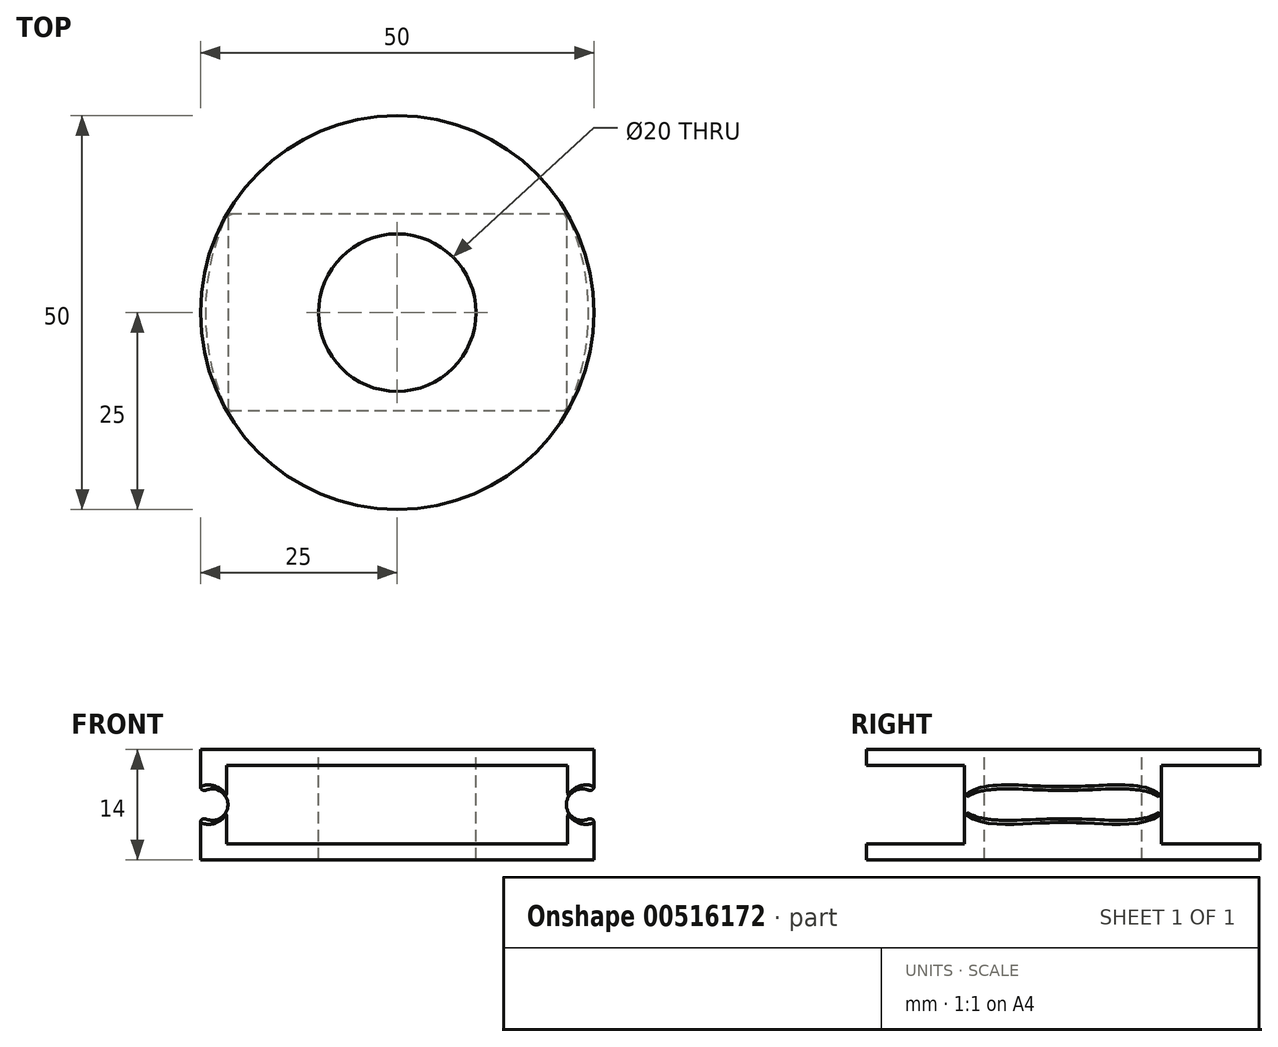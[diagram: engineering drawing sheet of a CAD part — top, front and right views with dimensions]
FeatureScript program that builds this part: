
annotation { "Feature Type Name" : "Feature", "Feature Type Description" : "" }
export const myFeature = defineFeature(function(context is Context, id is Id, definition is map)
    precondition{}
    {
        {
            var Q0;
            Q0=qCreatedBy(makeId("Right.planeOp"),FACE);
            var sketch = newSketch(context, id + "F0", { "sketchPlane" : qUnion([Q0])});
            skLineSegment(sketch, "E0.bottom", {"start": v(0, 0) * mm, "end": v(-50, 0) * mm});
            skLineSegment(sketch, "E0.top", {"start": v(0, 2) * mm, "end": v(-12.5, 2) * mm});
            skLineSegment(sketch, "E0.left", {"start": v(0, 0) * mm, "end": v(0, 2) * mm});
            skLineSegment(sketch, "E0.right", {"start": v(-50, 0) * mm, "end": v(-50, 2) * mm});
            skLineSegment(sketch, "E1.left", {"start": v(-12.5, 2) * mm, "end": v(-12.5, 12) * mm});
            skLineSegment(sketch, "E1.right", {"start": v(-37.5, 2) * mm, "end": v(-37.5, 12) * mm});
            skLineSegment(sketch, "E2.bottom", {"start": v(0, 12) * mm, "end": v(-12.5, 12) * mm});
            skLineSegment(sketch, "E2.top", {"start": v(0, 14) * mm, "end": v(-50, 14) * mm});
            skLineSegment(sketch, "E2.left", {"start": v(0, 12) * mm, "end": v(0, 14) * mm});
            skLineSegment(sketch, "E2.right", {"start": v(-50, 12) * mm, "end": v(-50, 14) * mm});
            skLineSegment(sketch, "E3.trimOffspring", {"start": v(-37.5, 12) * mm, "end": v(-50, 12) * mm});
            skLineSegment(sketch, "E4.trimOffspring", {"start": v(-37.5, 2) * mm, "end": v(-50, 2) * mm});
            skSolve(sketch);
        }
        {
            var Q0;
            Q0=makeQuery(id+"F0.imprint","IMPRINT",FACE,{"disambiguationData":[TD([[makeQuery(id+"F0.imprint","IMPRINT",EDGE,{"derivedFrom":sQuery(id+"F0.wireOp",EDGE,"E0.bottom")}),-1.0]])]});
            extrude(context, id + "F1", {"entities" : qUnion([Q0]), "depth" : 50 * mm, "offsetDistance" : 25 * mm});
        }
        {
            var Q0;
            Q0=makeQuery(id+"F1.opExtrude","SWEPT_FACE",FACE,{"disambiguationData":[OSD([sQuery(id+"F0.wireOp",EDGE,"E2.top")])]});
            var sketch = newSketch(context, id + "F2", { "sketchPlane" : qUnion([Q0])});
            skCircle(sketch, "E5", {"center": v(25, -25) * mm, "radius": 25 * mm});
            skPoint(sketch, "E6.trimOffspring.end.orphan", {"position": v(50, 0) * mm});
            skPoint(sketch, "E7.start.orphan", {"position": v(0, -50) * mm});
            skSolve(sketch);
        }
        {
            var Q0;
            Q0 = qSketchRegion(id + "F2", true);
            extrude(context, id + "F3", {"entities" : qUnion([Q0]), "operationType" : NewBodyOperationType.INTERSECT, "endBound" : BoundingType.THROUGH_ALL, "oppositeDirection" : true, "depth" : 25 * mm, "offsetDistance" : 25 * mm});
        }
        {
            var Q0;
            Q0=makeQuery(id+"F1.opExtrude","SWEPT_FACE",FACE,{"disambiguationData":[OSD([sQuery(id+"F0.wireOp",EDGE,"E2.top")])]});
            var sketch = newSketch(context, id + "F4", { "sketchPlane" : qUnion([Q0])});
            skCircle(sketch, "E8", {"center": v(25, -25) * mm, "radius": 10 * mm});
            skPoint(sketch, "E9.right.start.orphan", {"position": v(50, 0) * mm});
            skPoint(sketch, "E9.left.end.orphan", {"position": v(0, -50) * mm});
            skSolve(sketch);
        }
        {
            var Q0;
            Q0 = qSketchRegion(id + "F4", true);
            extrude(context, id + "F5", {"entities" : qUnion([Q0]), "operationType" : NewBodyOperationType.REMOVE, "endBound" : BoundingType.THROUGH_ALL, "oppositeDirection" : true, "depth" : 25 * mm, "offsetDistance" : 25 * mm});
        }
        {
            var Q0;
            Q0=makeQuery(id+"F1.opExtrude","SWEPT_FACE",FACE,{"disambiguationData":[OSD([sQuery(id+"F0.wireOp",EDGE,"E1.right")])]});
            var sketch = newSketch(context, id + "F6", { "sketchPlane" : qUnion([Q0])});
            skLineSegment(sketch, "E10", {"start": v(46.65, 7) * mm, "end": v(3.35, 7) * mm});
            skLineSegment(sketch, "E11", {"start": v(46.65, 7) * mm, "end": v(50, 7) * mm});
            skPoint(sketch, "E12", {"position": v(50, 7) * mm});
            skPoint(sketch, "E13", {"position": v(48.5, 7) * mm});
            skCircle(sketch, "E14", {"center": v(48.5, 7) * mm, "radius": 2 * mm});
            skSolve(sketch);
        }
        {
            var Q0;
            Q0 = qSketchRegion(id + "F6", true);
            extrude(context, id + "F7", {"entities" : qUnion([Q0]), "operationType" : NewBodyOperationType.REMOVE, "endBound" : BoundingType.THROUGH_ALL, "oppositeDirection" : true, "depth" : 25 * mm, "offsetDistance" : 25 * mm});
        }
        {
            var Q0;
            Q0=makeQuery(id+"F7.boolean.opBoolean","COPY",FACE,{"derivedFrom":makeQuery(id+"F7.opExtrude","SWEPT_FACE",FACE,{"disambiguationData":[OSD([sQuery(id+"F6.wireOp",EDGE,"E14")])]})});
            fillet(context, id + "F8", {"entities" : qUnion([Q0]), "radius" : 0.5 * mm, "tangentPropagation" : true, "allowEdgeOverflow" : false});
        }
        {
            var Q0;
            Q0=makeQuery(id+"F1.opExtrude","SWEPT_FACE",FACE,{"disambiguationData":[OSD([sQuery(id+"F0.wireOp",EDGE,"E1.right")])]});
            var sketch = newSketch(context, id + "F9", { "sketchPlane" : qUnion([Q0])});
            skLineSegment(sketch, "E15", {"start": v(3.35, 7) * mm, "end": v(1.5, 7) * mm});
            skPoint(sketch, "E16", {"position": v(0, 7) * mm});
            skPoint(sketch, "E17", {"position": v(1.5, 7) * mm});
            skCircle(sketch, "E18", {"center": v(1.5, 7) * mm, "radius": 2 * mm});
            skSolve(sketch);
        }
        {
            var Q0;
            Q0 = qSketchRegion(id + "F9", true);
            extrude(context, id + "F10", {"entities" : qUnion([Q0]), "operationType" : NewBodyOperationType.REMOVE, "endBound" : BoundingType.THROUGH_ALL, "oppositeDirection" : true, "depth" : 25 * mm, "offsetDistance" : 25 * mm});
        }
        {
            var Q0;
            Q0=makeQuery(id+"F10.boolean.opBoolean","COPY",FACE,{"derivedFrom":makeQuery(id+"F10.opExtrude","SWEPT_FACE",FACE,{"disambiguationData":[OSD([sQuery(id+"F9.wireOp",EDGE,"E18")])]})});
            fillet(context, id + "F11", {"entities" : qUnion([Q0]), "radius" : 0.5 * mm, "tangentPropagation" : true, "allowEdgeOverflow" : false});
        }
    });
